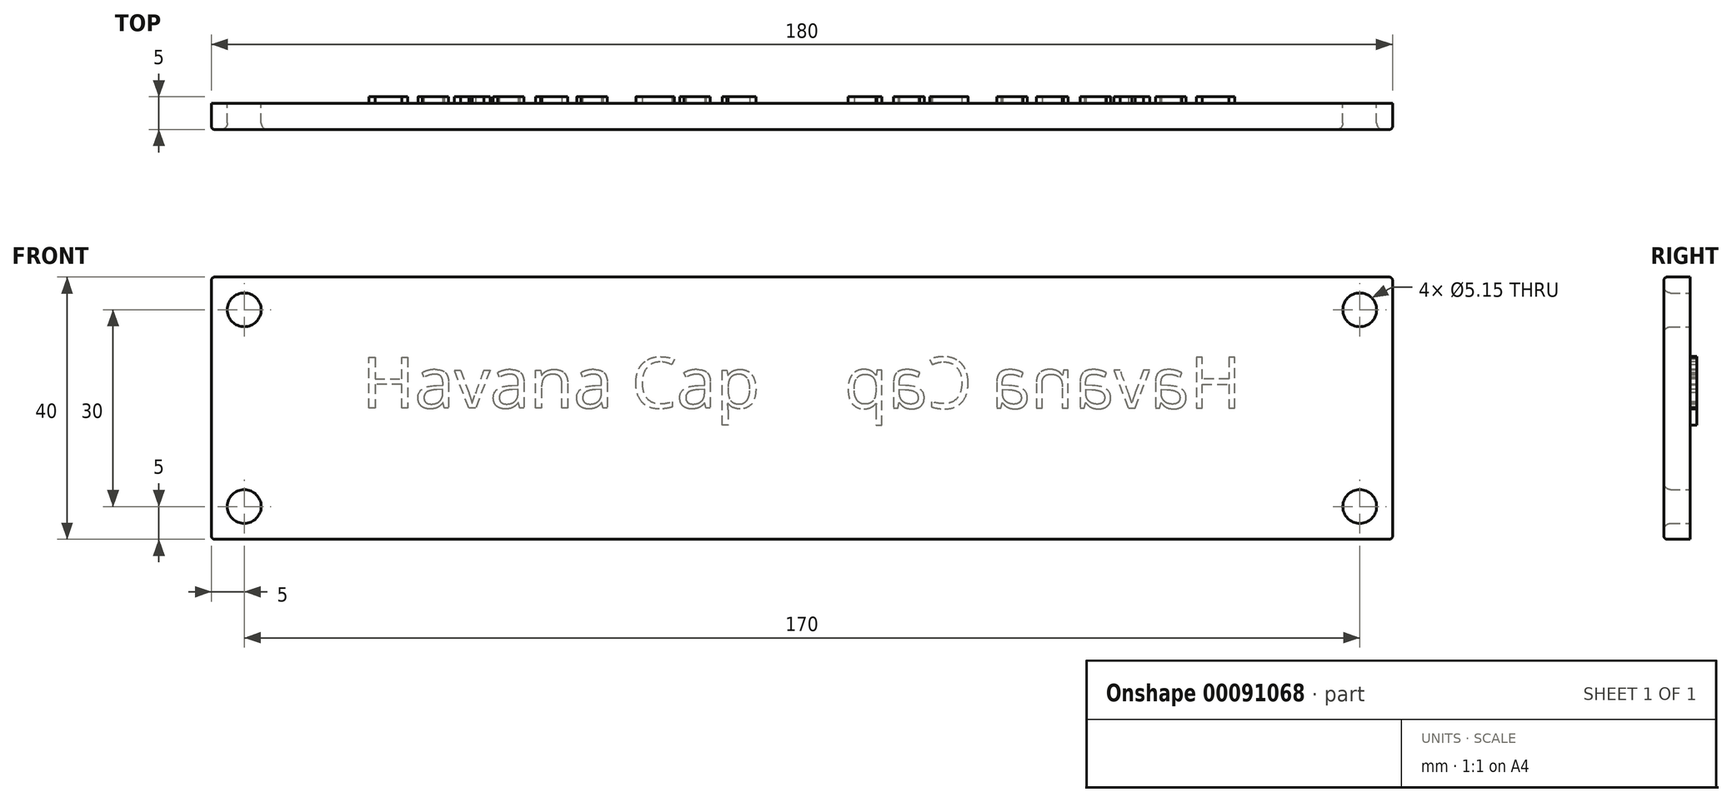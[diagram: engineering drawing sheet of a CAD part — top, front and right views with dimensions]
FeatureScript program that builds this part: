
annotation { "Feature Type Name" : "Feature", "Feature Type Description" : "" }
export const myFeature = defineFeature(function(context is Context, id is Id, definition is map)
    precondition{}
    {
        {
            var Q0;
            Q0=qCreatedBy(makeId("Front.planeOp"),FACE);
            var sketch = newSketch(context, id + "F0", { "sketchPlane" : qUnion([Q0])});
            skLineSegment(sketch, "E0.bottom", {"start": v(-90, -20) * mm, "end": v(90, -20) * mm});
            skLineSegment(sketch, "E0.top", {"start": v(-90, 20) * mm, "end": v(90, 20) * mm});
            skLineSegment(sketch, "E0.left", {"start": v(-90, -20) * mm, "end": v(-90, 20) * mm});
            skLineSegment(sketch, "E0.right", {"start": v(90, -20) * mm, "end": v(90, 20) * mm});
            skPoint(sketch, "E0.middle", {"position": v(0, 0) * mm});
            skCircle(sketch, "E1", {"center": v(-85, 15) * mm, "radius": 2.58 * mm});
            skPoint(sketch, "E2.start.orphan", {"position": v(-90, 0) * mm});
            skPoint(sketch, "E3.orphan", {"position": v(0, 20) * mm});
            skPoint(sketch, "E4.end.orphan", {"position": v(0, -20) * mm});
            skLineSegment(sketch, "E5", {"start": v(-90, 0) * mm, "end": v(0, 0) * mm, "construction": true});
            skLineSegment(sketch, "E6", {"start": v(0, 20) * mm, "end": v(0, -20) * mm, "construction": true});
            skCircle(sketch, "E7.MirrorC", {"center": v(-85, -15) * mm, "radius": 2.58 * mm});
            skCircle(sketch, "E8.MirrorC", {"center": v(85, 15) * mm, "radius": 2.58 * mm});
            skCircle(sketch, "E9.MirrorC", {"center": v(85, -15) * mm, "radius": 2.58 * mm});
            skSolve(sketch);
        }
        {
            var Q0;
            Q0=makeQuery(id+"F0.imprint","IMPRINT",FACE,{"disambiguationData":[TD([[makeQuery(id+"F0.imprint","IMPRINT",EDGE,{"derivedFrom":sQuery(id+"F0.wireOp",EDGE,"E0.bottom")}),1.0]])]});
            extrude(context, id + "F1", {"entities" : qUnion([Q0]), "depth" : 4 * mm});
        }
        {
            var Q0;
            Q0=makeQuery(id+"F1.opExtrude","CAP_EDGE",EDGE,{"disambiguationData":[OSD([sQuery(id+"F0.wireOp",EDGE,"E1")])],"isStart":false});
            var Q1;
            Q1=makeQuery(id+"F1.opExtrude","CAP_EDGE",EDGE,{"disambiguationData":[OSD([sQuery(id+"F0.wireOp",EDGE,"f5b72a5b-8583-449a-bdbf-9ac5a681e1fd0.MirrorC")])],"isStart":false});
            var Q2;
            Q2=makeQuery(id+"F1.opExtrude","CAP_EDGE",EDGE,{"disambiguationData":[OSD([sQuery(id+"F0.wireOp",EDGE,"2623e306-60f4-4522-aa65-1e3e8c2cf5b60.MirrorC")])],"isStart":false});
            var Q3;
            Q3=makeQuery(id+"F1.opExtrude","CAP_EDGE",EDGE,{"disambiguationData":[OSD([sQuery(id+"F0.wireOp",EDGE,"be81a34d-1d50-4ce7-a7a8-4484a1701fac0.MirrorC")])],"isStart":false});
            var Q4;
            Q4=makeQuery(id+"F1.opExtrude","CAP_EDGE",EDGE,{"disambiguationData":[OSD([sQuery(id+"F0.wireOp",EDGE,"E7.MirrorC")])],"isStart":false});
            var Q5;
            Q5=makeQuery(id+"F1.opExtrude","CAP_EDGE",EDGE,{"disambiguationData":[OSD([sQuery(id+"F0.wireOp",EDGE,"E8.MirrorC")])],"isStart":false});
            var Q6;
            Q6=makeQuery(id+"F1.opExtrude","CAP_EDGE",EDGE,{"disambiguationData":[OSD([sQuery(id+"F0.wireOp",EDGE,"E9.MirrorC")])],"isStart":false});
            fillet(context, id + "F2", {"entities" : qUnion([Q0, Q1, Q2, Q3, Q4, Q5, Q6]), "radius" : 1 * mm, "tangentPropagation" : true, "allowEdgeOverflow" : false});
        }
        {
            var Q0;
            Q0=makeQuery(id+"F1.opExtrude","CAP_EDGE",EDGE,{"disambiguationData":[OSD([sQuery(id+"F0.wireOp",EDGE,"E0.top")])],"isStart":false});
            var Q1;
            Q1=makeQuery(id+"F1.opExtrude","CAP_EDGE",EDGE,{"disambiguationData":[OSD([sQuery(id+"F0.wireOp",EDGE,"E0.left")])],"isStart":false});
            var Q2;
            Q2=makeQuery(id+"F1.opExtrude","CAP_EDGE",EDGE,{"disambiguationData":[OSD([sQuery(id+"F0.wireOp",EDGE,"E0.bottom")])],"isStart":false});
            var Q3;
            Q3=makeQuery(id+"F1.opExtrude","CAP_EDGE",EDGE,{"disambiguationData":[OSD([sQuery(id+"F0.wireOp",EDGE,"E0.right")])],"isStart":false});
            var Q4;
            Q4=makeQuery(id+"F1.opExtrude","SWEPT_EDGE",EDGE,{"disambiguationData":[OSD([sQuery(id+"F0.wireOp",EDGE,"E0.top"),sQuery(id+"F0.wireOp",EDGE,"E0.left")])]});
            var Q5;
            Q5=makeQuery(id+"F1.opExtrude","SWEPT_EDGE",EDGE,{"disambiguationData":[OSD([sQuery(id+"F0.wireOp",EDGE,"E0.bottom"),sQuery(id+"F0.wireOp",EDGE,"E0.left")])]});
            var Q6;
            Q6=makeQuery(id+"F1.opExtrude","SWEPT_EDGE",EDGE,{"disambiguationData":[OSD([sQuery(id+"F0.wireOp",EDGE,"E0.top"),sQuery(id+"F0.wireOp",EDGE,"E0.right")])]});
            var Q7;
            Q7=makeQuery(id+"F1.opExtrude","SWEPT_EDGE",EDGE,{"disambiguationData":[OSD([sQuery(id+"F0.wireOp",EDGE,"E0.bottom"),sQuery(id+"F0.wireOp",EDGE,"E0.right")])]});
            fillet(context, id + "F3", {"entities" : qUnion([Q0, Q1, Q2, Q3, Q4, Q5, Q6, Q7]), "radius" : .5 * mm, "tangentPropagation" : true, "allowEdgeOverflow" : false});
        }
        {
            var Q0;
            Q0=makeQuery(id+"F1.opExtrude","CAP_FACE",FACE,{"disambiguationData":[OSD([sQuery(id+"F0.wireOp",EDGE,"E0.bottom"),sQuery(id+"F0.wireOp",EDGE,"E0.top"),sQuery(id+"F0.wireOp",EDGE,"E0.left"),sQuery(id+"F0.wireOp",EDGE,"E0.right"),sQuery(id+"F0.wireOp",EDGE,"E1"),sQuery(id+"F0.wireOp",EDGE,"E7.MirrorC"),sQuery(id+"F0.wireOp",EDGE,"E8.MirrorC"),sQuery(id+"F0.wireOp",EDGE,"E9.MirrorC")])],"isStart":true});
            var sketch = newSketch(context, id + "F4", { "sketchPlane" : qUnion([Q0])});
            skText(sketch, "E10", { "text": "Havana Cap", "fontName": "OpenSans-Regular.ttf"});
            skLineSegment(sketch, "E11", {"start": v(0, 20) * mm, "end": v(0, -20) * mm, "construction": true});
            const initialGuessF4  = {"E10": [-0.06704, 0, 1, 0, 0.00782]};
            skSetInitialGuess(sketch, initialGuessF4);
            skSolve(sketch);
        }
        {
            var Q0;
            Q0=qSketchRegion(id+"F4",true);
            extrude(context, id + "F5", {"entities" : qUnion([Q0]), "operationType" : NewBodyOperationType.ADD, "depth" : 1 * mm});
        }
        {
            var Q0;
            Q0=makeQuery(id+"F1.opExtrude","SWEPT_BODY",BODY,{"disambiguationData":[OSD([sQuery(id+"F0.wireOp",EDGE,"E0.bottom"),sQuery(id+"F0.wireOp",EDGE,"E0.top"),sQuery(id+"F0.wireOp",EDGE,"E0.left"),sQuery(id+"F0.wireOp",EDGE,"E0.right"),sQuery(id+"F0.wireOp",EDGE,"E1"),sQuery(id+"F0.wireOp",EDGE,"E7.MirrorC"),sQuery(id+"F0.wireOp",EDGE,"E8.MirrorC"),sQuery(id+"F0.wireOp",EDGE,"E9.MirrorC")])]});
            var Q1;
            Q1=makeQuery(id+"F5.opExtrude","SWEPT_FACE",FACE,{"disambiguationData":[OSD([sQuery(id+"F4.wireOp",EDGE,"E10.sketch_text.stroke-94")])]});
            var Q2;
            Q2=makeQuery(id+"F5.opExtrude","SWEPT_FACE",FACE,{"disambiguationData":[OSD([sQuery(id+"F4.wireOp",EDGE,"E10.sketch_text.stroke-169")])]});
            var Q3;
            Q3=makeQuery(id+"F5.opExtrude","SWEPT_FACE",FACE,{"disambiguationData":[OSD([sQuery(id+"F4.wireOp",EDGE,"E10.sketch_text.stroke-185")])]});
            var Q4;
            Q4=makeQuery(id+"F5.opExtrude","SWEPT_FACE",FACE,{"disambiguationData":[OSD([sQuery(id+"F4.wireOp",EDGE,"E10.sketch_text.stroke-125")])]});
            var Q5;
            Q5=makeQuery(id+"F5.opExtrude","SWEPT_FACE",FACE,{"disambiguationData":[OSD([sQuery(id+"F4.wireOp",EDGE,"E10.sketch_text.stroke-155")])]});
            var Q6;
            Q6=makeQuery(id+"F5.opExtrude","SWEPT_FACE",FACE,{"disambiguationData":[OSD([sQuery(id+"F4.wireOp",EDGE,"E10.sketch_text.stroke-65")])]});
            var Q7;
            Q7=makeQuery(id+"F5.opExtrude","SWEPT_FACE",FACE,{"disambiguationData":[OSD([sQuery(id+"F4.wireOp",EDGE,"E10.sketch_text.stroke-81")])]});
            var Q8;
            Q8=makeQuery(id+"F5.opExtrude","SWEPT_FACE",FACE,{"disambiguationData":[OSD([sQuery(id+"F4.wireOp",EDGE,"E10.sketch_text.stroke-67")])]});
            var Q9;
            Q9=makeQuery(id+"F5.opExtrude","SWEPT_FACE",FACE,{"disambiguationData":[OSD([sQuery(id+"F4.wireOp",EDGE,"E10.sketch_text.stroke-99")])]});
            var Q10;
            Q10=makeQuery(id+"F5.opExtrude","SWEPT_FACE",FACE,{"disambiguationData":[OSD([sQuery(id+"F4.wireOp",EDGE,"E10.sketch_text.stroke-127")])]});
            var Q11;
            Q11=makeQuery(id+"F5.opExtrude","SWEPT_FACE",FACE,{"disambiguationData":[OSD([sQuery(id+"F4.wireOp",EDGE,"E10.sketch_text.stroke-10")])]});
            var Q12;
            Q12=makeQuery(id+"F5.opExtrude","CAP_FACE",FACE,{"disambiguationData":[OSD([sQuery(id+"F4.wireOp",EDGE,"E10.sketch_text.stroke-9"),sQuery(id+"F4.wireOp",EDGE,"E10.sketch_text.stroke-10"),sQuery(id+"F4.wireOp",EDGE,"E10.sketch_text.stroke-11"),sQuery(id+"F4.wireOp",EDGE,"E10.sketch_text.stroke-12")])],"isStart":false});
            var Q13;
            Q13=makeQuery(id+"F5.opExtrude","SWEPT_FACE",FACE,{"disambiguationData":[OSD([sQuery(id+"F4.wireOp",EDGE,"E10.sketch_text.stroke-154")])]});
            var Q14;
            Q14=makeQuery(id+"F5.opExtrude","SWEPT_FACE",FACE,{"disambiguationData":[OSD([sQuery(id+"F4.wireOp",EDGE,"E10.sketch_text.stroke-1")])]});
            var Q15;
            Q15=makeQuery(id+"F5.opExtrude","CAP_FACE",FACE,{"disambiguationData":[OSD([sQuery(id+"F4.wireOp",EDGE,"E10.sketch_text.stroke-124"),sQuery(id+"F4.wireOp",EDGE,"E10.sketch_text.stroke-125"),sQuery(id+"F4.wireOp",EDGE,"E10.sketch_text.stroke-126"),sQuery(id+"F4.wireOp",EDGE,"E10.sketch_text.stroke-127"),sQuery(id+"F4.wireOp",EDGE,"E10.sketch_text.stroke-128"),sQuery(id+"F4.wireOp",EDGE,"E10.sketch_text.stroke-129"),sQuery(id+"F4.wireOp",EDGE,"E10.sketch_text.stroke-130"),sQuery(id+"F4.wireOp",EDGE,"E10.sketch_text.stroke-131"),sQuery(id+"F4.wireOp",EDGE,"E10.sketch_text.stroke-132"),sQuery(id+"F4.wireOp",EDGE,"E10.sketch_text.stroke-133"),sQuery(id+"F4.wireOp",EDGE,"E10.sketch_text.stroke-134"),sQuery(id+"F4.wireOp",EDGE,"E10.sketch_text.stroke-135"),sQuery(id+"F4.wireOp",EDGE,"E10.sketch_text.stroke-136"),sQuery(id+"F4.wireOp",EDGE,"E10.sketch_text.stroke-137"),sQuery(id+"F4.wireOp",EDGE,"E10.sketch_text.stroke-138")])],"isStart":false});
            var Q16;
            Q16=makeQuery(id+"F5.opExtrude","CAP_FACE",FACE,{"disambiguationData":[OSD([sQuery(id+"F4.wireOp",EDGE,"E10.sketch_text.stroke-34"),sQuery(id+"F4.wireOp",EDGE,"E10.sketch_text.stroke-35"),sQuery(id+"F4.wireOp",EDGE,"E10.sketch_text.stroke-36"),sQuery(id+"F4.wireOp",EDGE,"E10.sketch_text.stroke-37"),sQuery(id+"F4.wireOp",EDGE,"E10.sketch_text.stroke-38"),sQuery(id+"F4.wireOp",EDGE,"E10.sketch_text.stroke-39"),sQuery(id+"F4.wireOp",EDGE,"E10.sketch_text.stroke-40"),sQuery(id+"F4.wireOp",EDGE,"E10.sketch_text.stroke-41"),sQuery(id+"F4.wireOp",EDGE,"E10.sketch_text.stroke-42"),sQuery(id+"F4.wireOp",EDGE,"E10.sketch_text.stroke-43"),sQuery(id+"F4.wireOp",EDGE,"E10.sketch_text.stroke-44"),sQuery(id+"F4.wireOp",EDGE,"E10.sketch_text.stroke-45"),sQuery(id+"F4.wireOp",EDGE,"E10.sketch_text.stroke-46"),sQuery(id+"F4.wireOp",EDGE,"E10.sketch_text.stroke-47"),sQuery(id+"F4.wireOp",EDGE,"E10.sketch_text.stroke-48"),sQuery(id+"F4.wireOp",EDGE,"E10.sketch_text.stroke-49"),sQuery(id+"F4.wireOp",EDGE,"E10.sketch_text.stroke-50"),sQuery(id+"F4.wireOp",EDGE,"E10.sketch_text.stroke-51"),sQuery(id+"F4.wireOp",EDGE,"E10.sketch_text.stroke-52"),sQuery(id+"F4.wireOp",EDGE,"E10.sketch_text.stroke-53"),sQuery(id+"F4.wireOp",EDGE,"E10.sketch_text.stroke-54"),sQuery(id+"F4.wireOp",EDGE,"E10.sketch_text.stroke-55"),sQuery(id+"F4.wireOp",EDGE,"E10.sketch_text.stroke-56"),sQuery(id+"F4.wireOp",EDGE,"E10.sketch_text.stroke-57"),sQuery(id+"F4.wireOp",EDGE,"E10.sketch_text.stroke-58"),sQuery(id+"F4.wireOp",EDGE,"E10.sketch_text.stroke-59"),sQuery(id+"F4.wireOp",EDGE,"E10.sketch_text.stroke-60")])],"isStart":false});
            var Q17;
            Q17=makeQuery(id+"F5.opExtrude","SWEPT_FACE",FACE,{"disambiguationData":[OSD([sQuery(id+"F4.wireOp",EDGE,"E10.sketch_text.stroke-50")])]});
            var Q18;
            Q18=makeQuery(id+"F5.opExtrude","SWEPT_FACE",FACE,{"disambiguationData":[OSD([sQuery(id+"F4.wireOp",EDGE,"E10.sketch_text.stroke-2")])]});
            var Q19;
            Q19=makeQuery(id+"F5.opExtrude","SWEPT_FACE",FACE,{"disambiguationData":[OSD([sQuery(id+"F4.wireOp",EDGE,"E10.sketch_text.stroke-3")])]});
            var Q20;
            Q20=makeQuery(id+"F5.opExtrude","SWEPT_FACE",FACE,{"disambiguationData":[OSD([sQuery(id+"F4.wireOp",EDGE,"E10.sketch_text.stroke-5")])]});
            var Q21;
            Q21=makeQuery(id+"F5.opExtrude","SWEPT_FACE",FACE,{"disambiguationData":[OSD([sQuery(id+"F4.wireOp",EDGE,"E10.sketch_text.stroke-8")])]});
            var Q22;
            Q22=makeQuery(id+"F5.opExtrude","SWEPT_FACE",FACE,{"disambiguationData":[OSD([sQuery(id+"F4.wireOp",EDGE,"E10.sketch_text.stroke-98")])]});
            var Q23;
            Q23=makeQuery(id+"F5.opExtrude","SWEPT_FACE",FACE,{"disambiguationData":[OSD([sQuery(id+"F4.wireOp",EDGE,"E10.sketch_text.stroke-66")])]});
            var Q24;
            Q24=makeQuery(id+"F5.opExtrude","SWEPT_FACE",FACE,{"disambiguationData":[OSD([sQuery(id+"F4.wireOp",EDGE,"E10.sketch_text.stroke-153")])]});
            var Q25;
            Q25=makeQuery(id+"F5.opExtrude","SWEPT_FACE",FACE,{"disambiguationData":[OSD([sQuery(id+"F4.wireOp",EDGE,"E10.sketch_text.stroke-126")])]});
            var Q26;
            Q26=makeQuery(id+"F5.opExtrude","SWEPT_FACE",FACE,{"disambiguationData":[OSD([sQuery(id+"F4.wireOp",EDGE,"E10.sketch_text.stroke-183")])]});
            var Q27;
            Q27=makeQuery(id+"F5.opExtrude","SWEPT_FACE",FACE,{"disambiguationData":[OSD([sQuery(id+"F4.wireOp",EDGE,"E10.sketch_text.stroke-109")])]});
            var Q28;
            Q28=makeQuery(id+"F5.opExtrude","SWEPT_FACE",FACE,{"disambiguationData":[OSD([sQuery(id+"F4.wireOp",EDGE,"E10.sketch_text.stroke-186")])]});
            var Q29;
            Q29=makeQuery(id+"F5.opExtrude","SWEPT_FACE",FACE,{"disambiguationData":[OSD([sQuery(id+"F4.wireOp",EDGE,"E10.sketch_text.stroke-79")])]});
            var Q30;
            Q30=makeQuery(id+"F5.opExtrude","SWEPT_FACE",FACE,{"disambiguationData":[OSD([sQuery(id+"F4.wireOp",EDGE,"E10.sketch_text.stroke-110")])]});
            var Q31;
            Q31=makeQuery(id+"F5.opExtrude","SWEPT_FACE",FACE,{"disambiguationData":[OSD([sQuery(id+"F4.wireOp",EDGE,"E10.sketch_text.stroke-38")])]});
            var Q32;
            Q32=makeQuery(id+"F5.opExtrude","SWEPT_FACE",FACE,{"disambiguationData":[OSD([sQuery(id+"F4.wireOp",EDGE,"E10.sketch_text.stroke-24")])]});
            var Q33;
            Q33=makeQuery(id+"F5.opExtrude","SWEPT_FACE",FACE,{"disambiguationData":[OSD([sQuery(id+"F4.wireOp",EDGE,"E10.sketch_text.stroke-12")])]});
            var Q34;
            Q34=makeQuery(id+"F5.opExtrude","SWEPT_FACE",FACE,{"disambiguationData":[OSD([sQuery(id+"F4.wireOp",EDGE,"E10.sketch_text.stroke-100")])]});
            var Q35;
            Q35=makeQuery(id+"F5.opExtrude","SWEPT_FACE",FACE,{"disambiguationData":[OSD([sQuery(id+"F4.wireOp",EDGE,"E10.sketch_text.stroke-158")])]});
            var Q36;
            Q36=makeQuery(id+"F5.opExtrude","SWEPT_FACE",FACE,{"disambiguationData":[OSD([sQuery(id+"F4.wireOp",EDGE,"E10.sketch_text.stroke-142")])]});
            var Q37;
            Q37=makeQuery(id+"F5.opExtrude","SWEPT_FACE",FACE,{"disambiguationData":[OSD([sQuery(id+"F4.wireOp",EDGE,"E10.sketch_text.stroke-54")])]});
            var Q38;
            Q38=makeQuery(id+"F5.opExtrude","SWEPT_FACE",FACE,{"disambiguationData":[OSD([sQuery(id+"F4.wireOp",EDGE,"E10.sketch_text.stroke-25")])]});
            var Q39;
            Q39=makeQuery(id+"F5.opExtrude","SWEPT_FACE",FACE,{"disambiguationData":[OSD([sQuery(id+"F4.wireOp",EDGE,"E10.sketch_text.stroke-101")])]});
            var Q40;
            Q40=makeQuery(id+"F5.opExtrude","SWEPT_FACE",FACE,{"disambiguationData":[OSD([sQuery(id+"F4.wireOp",EDGE,"E10.sketch_text.stroke-69")])]});
            var Q41;
            Q41=makeQuery(id+"F5.opExtrude","SWEPT_FACE",FACE,{"disambiguationData":[OSD([sQuery(id+"F4.wireOp",EDGE,"E10.sketch_text.stroke-159")])]});
            var Q42;
            Q42=makeQuery(id+"F5.opExtrude","SWEPT_FACE",FACE,{"disambiguationData":[OSD([sQuery(id+"F4.wireOp",EDGE,"E10.sketch_text.stroke-85")])]});
            var Q43;
            Q43=makeQuery(id+"F5.opExtrude","SWEPT_FACE",FACE,{"disambiguationData":[OSD([sQuery(id+"F4.wireOp",EDGE,"E10.sketch_text.stroke-173")])]});
            var Q44;
            Q44=makeQuery(id+"F5.opExtrude","SWEPT_FACE",FACE,{"disambiguationData":[OSD([sQuery(id+"F4.wireOp",EDGE,"E10.sketch_text.stroke-40")])]});
            var Q45;
            Q45=makeQuery(id+"F5.opExtrude","SWEPT_FACE",FACE,{"disambiguationData":[OSD([sQuery(id+"F4.wireOp",EDGE,"E10.sketch_text.stroke-102")])]});
            var Q46;
            Q46=makeQuery(id+"F5.opExtrude","SWEPT_FACE",FACE,{"disambiguationData":[OSD([sQuery(id+"F4.wireOp",EDGE,"E10.sketch_text.stroke-86")])]});
            var Q47;
            Q47=makeQuery(id+"F5.opExtrude","SWEPT_FACE",FACE,{"disambiguationData":[OSD([sQuery(id+"F4.wireOp",EDGE,"E10.sketch_text.stroke-130")])]});
            var Q48;
            Q48=makeQuery(id+"F5.opExtrude","SWEPT_FACE",FACE,{"disambiguationData":[OSD([sQuery(id+"F4.wireOp",EDGE,"E10.sketch_text.stroke-103")])]});
            var Q49;
            Q49=makeQuery(id+"F5.opExtrude","SWEPT_FACE",FACE,{"disambiguationData":[OSD([sQuery(id+"F4.wireOp",EDGE,"E10.sketch_text.stroke-87")])]});
            var Q50;
            Q50=makeQuery(id+"F5.opExtrude","SWEPT_FACE",FACE,{"disambiguationData":[OSD([sQuery(id+"F4.wireOp",EDGE,"E10.sketch_text.stroke-145")])]});
            var Q51;
            Q51=makeQuery(id+"F5.opExtrude","SWEPT_FACE",FACE,{"disambiguationData":[OSD([sQuery(id+"F4.wireOp",EDGE,"E10.sketch_text.stroke-131")])]});
            var Q52;
            Q52=makeQuery(id+"F5.opExtrude","SWEPT_FACE",FACE,{"disambiguationData":[OSD([sQuery(id+"F4.wireOp",EDGE,"E10.sketch_text.stroke-28")])]});
            var Q53;
            Q53=makeQuery(id+"F5.opExtrude","SWEPT_FACE",FACE,{"disambiguationData":[OSD([sQuery(id+"F4.wireOp",EDGE,"E10.sketch_text.stroke-14")])]});
            var Q54;
            Q54=makeQuery(id+"F5.opExtrude","SWEPT_FACE",FACE,{"disambiguationData":[OSD([sQuery(id+"F4.wireOp",EDGE,"E10.sketch_text.stroke-88")])]});
            var Q55;
            Q55=makeQuery(id+"F5.opExtrude","SWEPT_FACE",FACE,{"disambiguationData":[OSD([sQuery(id+"F4.wireOp",EDGE,"E10.sketch_text.stroke-162")])]});
            var Q56;
            Q56=makeQuery(id+"F5.opExtrude","SWEPT_FACE",FACE,{"disambiguationData":[OSD([sQuery(id+"F4.wireOp",EDGE,"E10.sketch_text.stroke-176")])]});
            var Q57;
            Q57=makeQuery(id+"F5.opExtrude","SWEPT_FACE",FACE,{"disambiguationData":[OSD([sQuery(id+"F4.wireOp",EDGE,"E10.sketch_text.stroke-73")])]});
            var Q58;
            Q58=makeQuery(id+"F5.opExtrude","SWEPT_FACE",FACE,{"disambiguationData":[OSD([sQuery(id+"F4.wireOp",EDGE,"E10.sketch_text.stroke-59")])]});
            var Q59;
            Q59=makeQuery(id+"F5.opExtrude","SWEPT_FACE",FACE,{"disambiguationData":[OSD([sQuery(id+"F4.wireOp",EDGE,"E10.sketch_text.stroke-133")])]});
            var Q60;
            Q60=makeQuery(id+"F5.opExtrude","SWEPT_FACE",FACE,{"disambiguationData":[OSD([sQuery(id+"F4.wireOp",EDGE,"E10.sketch_text.stroke-119")])]});
            var Q61;
            Q61=makeQuery(id+"F5.opExtrude","SWEPT_FACE",FACE,{"disambiguationData":[OSD([sQuery(id+"F4.wireOp",EDGE,"E10.sketch_text.stroke-74")])]});
            var Q62;
            Q62=makeQuery(id+"F5.opExtrude","SWEPT_FACE",FACE,{"disambiguationData":[OSD([sQuery(id+"F4.wireOp",EDGE,"E10.sketch_text.stroke-44")])]});
            var Q63;
            Q63=makeQuery(id+"F5.opExtrude","SWEPT_FACE",FACE,{"disambiguationData":[OSD([sQuery(id+"F4.wireOp",EDGE,"E10.sketch_text.stroke-120")])]});
            var Q64;
            Q64=makeQuery(id+"F5.opExtrude","SWEPT_FACE",FACE,{"disambiguationData":[OSD([sQuery(id+"F4.wireOp",EDGE,"E10.sketch_text.stroke-90")])]});
            var Q65;
            Q65=makeQuery(id+"F5.opExtrude","SWEPT_FACE",FACE,{"disambiguationData":[OSD([sQuery(id+"F4.wireOp",EDGE,"E10.sketch_text.stroke-178")])]});
            var Q66;
            Q66=makeQuery(id+"F5.opExtrude","SWEPT_FACE",FACE,{"disambiguationData":[OSD([sQuery(id+"F4.wireOp",EDGE,"E10.sketch_text.stroke-45")])]});
            var Q67;
            Q67=makeQuery(id+"F5.opExtrude","SWEPT_FACE",FACE,{"disambiguationData":[OSD([sQuery(id+"F4.wireOp",EDGE,"E10.sketch_text.stroke-31")])]});
            var Q68;
            Q68=makeQuery(id+"F5.opExtrude","SWEPT_FACE",FACE,{"disambiguationData":[OSD([sQuery(id+"F4.wireOp",EDGE,"E10.sketch_text.stroke-135")])]});
            var Q69;
            Q69=makeQuery(id+"F5.opExtrude","SWEPT_FACE",FACE,{"disambiguationData":[OSD([sQuery(id+"F4.wireOp",EDGE,"E10.sketch_text.stroke-179")])]});
            var Q70;
            Q70=makeQuery(id+"F5.opExtrude","SWEPT_FACE",FACE,{"disambiguationData":[OSD([sQuery(id+"F4.wireOp",EDGE,"E10.sketch_text.stroke-165")])]});
            var Q71;
            Q71=makeQuery(id+"F5.opExtrude","SWEPT_FACE",FACE,{"disambiguationData":[OSD([sQuery(id+"F4.wireOp",EDGE,"E10.sketch_text.stroke-149")])]});
            var Q72;
            Q72=makeQuery(id+"F5.opExtrude","SWEPT_FACE",FACE,{"disambiguationData":[OSD([sQuery(id+"F4.wireOp",EDGE,"E10.sketch_text.stroke-136")])]});
            var Q73;
            Q73=makeQuery(id+"F5.opExtrude","SWEPT_FACE",FACE,{"disambiguationData":[OSD([sQuery(id+"F4.wireOp",EDGE,"E10.sketch_text.stroke-122")])]});
            var Q74;
            Q74=makeQuery(id+"F5.opExtrude","SWEPT_FACE",FACE,{"disambiguationData":[OSD([sQuery(id+"F4.wireOp",EDGE,"E10.sketch_text.stroke-106")])]});
            var Q75;
            Q75=makeQuery(id+"F5.opExtrude","SWEPT_FACE",FACE,{"disambiguationData":[OSD([sQuery(id+"F4.wireOp",EDGE,"E10.sketch_text.stroke-180")])]});
            var Q76;
            Q76=makeQuery(id+"F5.opExtrude","SWEPT_FACE",FACE,{"disambiguationData":[OSD([sQuery(id+"F4.wireOp",EDGE,"E10.sketch_text.stroke-166")])]});
            var Q77;
            Q77=makeQuery(id+"F5.opExtrude","SWEPT_FACE",FACE,{"disambiguationData":[OSD([sQuery(id+"F4.wireOp",EDGE,"E10.sketch_text.stroke-150")])]});
            var Q78;
            Q78=makeQuery(id+"F5.opExtrude","SWEPT_FACE",FACE,{"disambiguationData":[OSD([sQuery(id+"F4.wireOp",EDGE,"E10.sketch_text.stroke-76")])]});
            var Q79;
            Q79=makeQuery(id+"F5.opExtrude","SWEPT_FACE",FACE,{"disambiguationData":[OSD([sQuery(id+"F4.wireOp",EDGE,"E10.sketch_text.stroke-32")])]});
            var Q80;
            Q80=makeQuery(id+"F5.opExtrude","SWEPT_FACE",FACE,{"disambiguationData":[OSD([sQuery(id+"F4.wireOp",EDGE,"E10.sketch_text.stroke-181")])]});
            var Q81;
            Q81=makeQuery(id+"F5.opExtrude","SWEPT_FACE",FACE,{"disambiguationData":[OSD([sQuery(id+"F4.wireOp",EDGE,"E10.sketch_text.stroke-47")])]});
            var Q82;
            Q82=makeQuery(id+"F5.opExtrude","SWEPT_FACE",FACE,{"disambiguationData":[OSD([sQuery(id+"F4.wireOp",EDGE,"E10.sketch_text.stroke-123")])]});
            var Q83;
            Q83=makeQuery(id+"F5.opExtrude","SWEPT_FACE",FACE,{"disambiguationData":[OSD([sQuery(id+"F4.wireOp",EDGE,"E10.sketch_text.stroke-107")])]});
            var Q84;
            Q84=makeQuery(id+"F5.opExtrude","SWEPT_FACE",FACE,{"disambiguationData":[OSD([sQuery(id+"F4.wireOp",EDGE,"E10.sketch_text.stroke-48")])]});
            var Q85;
            Q85=makeQuery(id+"F5.opExtrude","SWEPT_FACE",FACE,{"disambiguationData":[OSD([sQuery(id+"F4.wireOp",EDGE,"E10.sketch_text.stroke-124")])]});
            var Q86;
            Q86=makeQuery(id+"F5.opExtrude","SWEPT_FACE",FACE,{"disambiguationData":[OSD([sQuery(id+"F4.wireOp",EDGE,"E10.sketch_text.stroke-108")])]});
            var Q87;
            Q87=makeQuery(id+"F5.opExtrude","CAP_FACE",FACE,{"disambiguationData":[OSD([sQuery(id+"F4.wireOp",EDGE,"E10.sketch_text.stroke-139"),sQuery(id+"F4.wireOp",EDGE,"E10.sketch_text.stroke-140"),sQuery(id+"F4.wireOp",EDGE,"E10.sketch_text.stroke-141"),sQuery(id+"F4.wireOp",EDGE,"E10.sketch_text.stroke-142"),sQuery(id+"F4.wireOp",EDGE,"E10.sketch_text.stroke-143"),sQuery(id+"F4.wireOp",EDGE,"E10.sketch_text.stroke-144"),sQuery(id+"F4.wireOp",EDGE,"E10.sketch_text.stroke-145"),sQuery(id+"F4.wireOp",EDGE,"E10.sketch_text.stroke-146"),sQuery(id+"F4.wireOp",EDGE,"E10.sketch_text.stroke-147"),sQuery(id+"F4.wireOp",EDGE,"E10.sketch_text.stroke-148"),sQuery(id+"F4.wireOp",EDGE,"E10.sketch_text.stroke-149"),sQuery(id+"F4.wireOp",EDGE,"E10.sketch_text.stroke-150"),sQuery(id+"F4.wireOp",EDGE,"E10.sketch_text.stroke-151"),sQuery(id+"F4.wireOp",EDGE,"E10.sketch_text.stroke-152"),sQuery(id+"F4.wireOp",EDGE,"E10.sketch_text.stroke-153"),sQuery(id+"F4.wireOp",EDGE,"E10.sketch_text.stroke-154"),sQuery(id+"F4.wireOp",EDGE,"E10.sketch_text.stroke-155"),sQuery(id+"F4.wireOp",EDGE,"E10.sketch_text.stroke-156"),sQuery(id+"F4.wireOp",EDGE,"E10.sketch_text.stroke-157"),sQuery(id+"F4.wireOp",EDGE,"E10.sketch_text.stroke-158"),sQuery(id+"F4.wireOp",EDGE,"E10.sketch_text.stroke-159"),sQuery(id+"F4.wireOp",EDGE,"E10.sketch_text.stroke-160"),sQuery(id+"F4.wireOp",EDGE,"E10.sketch_text.stroke-161"),sQuery(id+"F4.wireOp",EDGE,"E10.sketch_text.stroke-162"),sQuery(id+"F4.wireOp",EDGE,"E10.sketch_text.stroke-163"),sQuery(id+"F4.wireOp",EDGE,"E10.sketch_text.stroke-164"),sQuery(id+"F4.wireOp",EDGE,"E10.sketch_text.stroke-165")])],"isStart":false});
            var Q88;
            Q88=makeQuery(id+"F5.opExtrude","CAP_FACE",FACE,{"disambiguationData":[OSD([sQuery(id+"F4.wireOp",EDGE,"E10.sketch_text.stroke-21"),sQuery(id+"F4.wireOp",EDGE,"E10.sketch_text.stroke-22"),sQuery(id+"F4.wireOp",EDGE,"E10.sketch_text.stroke-23"),sQuery(id+"F4.wireOp",EDGE,"E10.sketch_text.stroke-24"),sQuery(id+"F4.wireOp",EDGE,"E10.sketch_text.stroke-25"),sQuery(id+"F4.wireOp",EDGE,"E10.sketch_text.stroke-26"),sQuery(id+"F4.wireOp",EDGE,"E10.sketch_text.stroke-27"),sQuery(id+"F4.wireOp",EDGE,"E10.sketch_text.stroke-28"),sQuery(id+"F4.wireOp",EDGE,"E10.sketch_text.stroke-29"),sQuery(id+"F4.wireOp",EDGE,"E10.sketch_text.stroke-30"),sQuery(id+"F4.wireOp",EDGE,"E10.sketch_text.stroke-31"),sQuery(id+"F4.wireOp",EDGE,"E10.sketch_text.stroke-32"),sQuery(id+"F4.wireOp",EDGE,"E10.sketch_text.stroke-33")])],"isStart":false});
            var Q89;
            Q89=makeQuery(id+"F5.opExtrude","SWEPT_FACE",FACE,{"disambiguationData":[OSD([sQuery(id+"F4.wireOp",EDGE,"E10.sketch_text.stroke-113")])]});
            var Q90;
            Q90=makeQuery(id+"F5.opExtrude","SWEPT_FACE",FACE,{"disambiguationData":[OSD([sQuery(id+"F4.wireOp",EDGE,"E10.sketch_text.stroke-37")])]});
            var Q91;
            Q91=makeQuery(id+"F5.opExtrude","SWEPT_FACE",FACE,{"disambiguationData":[OSD([sQuery(id+"F4.wireOp",EDGE,"E10.sketch_text.stroke-187")])]});
            var Q92;
            Q92=makeQuery(id+"F5.opExtrude","SWEPT_FACE",FACE,{"disambiguationData":[OSD([sQuery(id+"F4.wireOp",EDGE,"E10.sketch_text.stroke-0")])]});
            var Q93;
            Q93=makeQuery(id+"F5.opExtrude","SWEPT_FACE",FACE,{"disambiguationData":[OSD([sQuery(id+"F4.wireOp",EDGE,"E10.sketch_text.stroke-4")])]});
            var Q94;
            Q94=makeQuery(id+"F5.opExtrude","SWEPT_FACE",FACE,{"disambiguationData":[OSD([sQuery(id+"F4.wireOp",EDGE,"E10.sketch_text.stroke-82")])]});
            var Q95;
            Q95=makeQuery(id+"F5.opExtrude","SWEPT_FACE",FACE,{"disambiguationData":[OSD([sQuery(id+"F4.wireOp",EDGE,"E10.sketch_text.stroke-52")])]});
            var Q96;
            Q96=makeQuery(id+"F5.opExtrude","SWEPT_FACE",FACE,{"disambiguationData":[OSD([sQuery(id+"F4.wireOp",EDGE,"E10.sketch_text.stroke-49")])]});
            var Q97;
            Q97=makeQuery(id+"F5.opExtrude","SWEPT_FACE",FACE,{"disambiguationData":[OSD([sQuery(id+"F4.wireOp",EDGE,"E10.sketch_text.stroke-63")])]});
            var Q98;
            Q98=makeQuery(id+"F5.opExtrude","SWEPT_FACE",FACE,{"disambiguationData":[OSD([sQuery(id+"F4.wireOp",EDGE,"E10.sketch_text.stroke-21")])]});
            var Q99;
            Q99=makeQuery(id+"F5.opExtrude","SWEPT_FACE",FACE,{"disambiguationData":[OSD([sQuery(id+"F4.wireOp",EDGE,"E10.sketch_text.stroke-128")])]});
            var Q100;
            Q100=makeQuery(id+"F5.opExtrude","SWEPT_FACE",FACE,{"disambiguationData":[OSD([sQuery(id+"F4.wireOp",EDGE,"E10.sketch_text.stroke-55")])]});
            var Q101;
            Q101=makeQuery(id+"F5.opExtrude","SWEPT_FACE",FACE,{"disambiguationData":[OSD([sQuery(id+"F4.wireOp",EDGE,"E10.sketch_text.stroke-26")])]});
            var Q102;
            Q102=makeQuery(id+"F5.opExtrude","SWEPT_FACE",FACE,{"disambiguationData":[OSD([sQuery(id+"F4.wireOp",EDGE,"E10.sketch_text.stroke-174")])]});
            var Q103;
            Q103=makeQuery(id+"F5.opExtrude","SWEPT_FACE",FACE,{"disambiguationData":[OSD([sQuery(id+"F4.wireOp",EDGE,"E10.sketch_text.stroke-104")])]});
            var Q104;
            Q104=makeQuery(id+"F5.opExtrude","SWEPT_FACE",FACE,{"disambiguationData":[OSD([sQuery(id+"F4.wireOp",EDGE,"E10.sketch_text.stroke-72")])]});
            var Q105;
            Q105=makeQuery(id+"F5.opExtrude","SWEPT_FACE",FACE,{"disambiguationData":[OSD([sQuery(id+"F4.wireOp",EDGE,"E10.sketch_text.stroke-132")])]});
            var Q106;
            Q106=makeQuery(id+"F5.opExtrude","SWEPT_FACE",FACE,{"disambiguationData":[OSD([sQuery(id+"F4.wireOp",EDGE,"E10.sketch_text.stroke-43")])]});
            var Q107;
            Q107=makeQuery(id+"F5.opExtrude","SWEPT_FACE",FACE,{"disambiguationData":[OSD([sQuery(id+"F4.wireOp",EDGE,"E10.sketch_text.stroke-15")])]});
            var Q108;
            Q108=makeQuery(id+"F5.opExtrude","SWEPT_FACE",FACE,{"disambiguationData":[OSD([sQuery(id+"F4.wireOp",EDGE,"E10.sketch_text.stroke-89")])]});
            var Q109;
            Q109=makeQuery(id+"F5.opExtrude","SWEPT_FACE",FACE,{"disambiguationData":[OSD([sQuery(id+"F4.wireOp",EDGE,"E10.sketch_text.stroke-163")])]});
            var Q110;
            Q110=makeQuery(id+"F5.opExtrude","SWEPT_FACE",FACE,{"disambiguationData":[OSD([sQuery(id+"F4.wireOp",EDGE,"E10.sketch_text.stroke-30")])]});
            var Q111;
            Q111=makeQuery(id+"F5.opExtrude","SWEPT_FACE",FACE,{"disambiguationData":[OSD([sQuery(id+"F4.wireOp",EDGE,"E10.sketch_text.stroke-134")])]});
            var Q112;
            Q112=makeQuery(id+"F5.opExtrude","SWEPT_FACE",FACE,{"disambiguationData":[OSD([sQuery(id+"F4.wireOp",EDGE,"E10.sketch_text.stroke-121")])]});
            var Q113;
            Q113=makeQuery(id+"F5.opExtrude","CAP_FACE",FACE,{"disambiguationData":[OSD([sQuery(id+"F4.wireOp",EDGE,"E10.sketch_text.stroke-105"),sQuery(id+"F4.wireOp",EDGE,"E10.sketch_text.stroke-106"),sQuery(id+"F4.wireOp",EDGE,"E10.sketch_text.stroke-107"),sQuery(id+"F4.wireOp",EDGE,"E10.sketch_text.stroke-108"),sQuery(id+"F4.wireOp",EDGE,"E10.sketch_text.stroke-109"),sQuery(id+"F4.wireOp",EDGE,"E10.sketch_text.stroke-110"),sQuery(id+"F4.wireOp",EDGE,"E10.sketch_text.stroke-111"),sQuery(id+"F4.wireOp",EDGE,"E10.sketch_text.stroke-112"),sQuery(id+"F4.wireOp",EDGE,"E10.sketch_text.stroke-113"),sQuery(id+"F4.wireOp",EDGE,"E10.sketch_text.stroke-114"),sQuery(id+"F4.wireOp",EDGE,"E10.sketch_text.stroke-115"),sQuery(id+"F4.wireOp",EDGE,"E10.sketch_text.stroke-116"),sQuery(id+"F4.wireOp",EDGE,"E10.sketch_text.stroke-117"),sQuery(id+"F4.wireOp",EDGE,"E10.sketch_text.stroke-118"),sQuery(id+"F4.wireOp",EDGE,"E10.sketch_text.stroke-119"),sQuery(id+"F4.wireOp",EDGE,"E10.sketch_text.stroke-120"),sQuery(id+"F4.wireOp",EDGE,"E10.sketch_text.stroke-121"),sQuery(id+"F4.wireOp",EDGE,"E10.sketch_text.stroke-122"),sQuery(id+"F4.wireOp",EDGE,"E10.sketch_text.stroke-123")])],"isStart":false});
            var Q114;
            Q114=makeQuery(id+"F5.opExtrude","SWEPT_FACE",FACE,{"disambiguationData":[OSD([sQuery(id+"F4.wireOp",EDGE,"E10.sketch_text.stroke-92")])]});
            var Q115;
            Q115=makeQuery(id+"F5.opExtrude","SWEPT_FACE",FACE,{"disambiguationData":[OSD([sQuery(id+"F4.wireOp",EDGE,"E10.sketch_text.stroke-46")])]});
            var Q116;
            Q116=makeQuery(id+"F5.opExtrude","CAP_FACE",FACE,{"disambiguationData":[OSD([sQuery(id+"F4.wireOp",EDGE,"E10.sketch_text.stroke-61"),sQuery(id+"F4.wireOp",EDGE,"E10.sketch_text.stroke-62"),sQuery(id+"F4.wireOp",EDGE,"E10.sketch_text.stroke-63"),sQuery(id+"F4.wireOp",EDGE,"E10.sketch_text.stroke-64"),sQuery(id+"F4.wireOp",EDGE,"E10.sketch_text.stroke-65"),sQuery(id+"F4.wireOp",EDGE,"E10.sketch_text.stroke-66"),sQuery(id+"F4.wireOp",EDGE,"E10.sketch_text.stroke-67"),sQuery(id+"F4.wireOp",EDGE,"E10.sketch_text.stroke-68"),sQuery(id+"F4.wireOp",EDGE,"E10.sketch_text.stroke-69"),sQuery(id+"F4.wireOp",EDGE,"E10.sketch_text.stroke-70"),sQuery(id+"F4.wireOp",EDGE,"E10.sketch_text.stroke-71"),sQuery(id+"F4.wireOp",EDGE,"E10.sketch_text.stroke-72"),sQuery(id+"F4.wireOp",EDGE,"E10.sketch_text.stroke-73"),sQuery(id+"F4.wireOp",EDGE,"E10.sketch_text.stroke-74"),sQuery(id+"F4.wireOp",EDGE,"E10.sketch_text.stroke-75"),sQuery(id+"F4.wireOp",EDGE,"E10.sketch_text.stroke-76"),sQuery(id+"F4.wireOp",EDGE,"E10.sketch_text.stroke-77"),sQuery(id+"F4.wireOp",EDGE,"E10.sketch_text.stroke-78"),sQuery(id+"F4.wireOp",EDGE,"E10.sketch_text.stroke-79"),sQuery(id+"F4.wireOp",EDGE,"E10.sketch_text.stroke-80"),sQuery(id+"F4.wireOp",EDGE,"E10.sketch_text.stroke-81"),sQuery(id+"F4.wireOp",EDGE,"E10.sketch_text.stroke-82"),sQuery(id+"F4.wireOp",EDGE,"E10.sketch_text.stroke-83"),sQuery(id+"F4.wireOp",EDGE,"E10.sketch_text.stroke-84"),sQuery(id+"F4.wireOp",EDGE,"E10.sketch_text.stroke-85"),sQuery(id+"F4.wireOp",EDGE,"E10.sketch_text.stroke-86"),sQuery(id+"F4.wireOp",EDGE,"E10.sketch_text.stroke-87"),sQuery(id+"F4.wireOp",EDGE,"E10.sketch_text.stroke-88"),sQuery(id+"F4.wireOp",EDGE,"E10.sketch_text.stroke-89"),sQuery(id+"F4.wireOp",EDGE,"E10.sketch_text.stroke-90"),sQuery(id+"F4.wireOp",EDGE,"E10.sketch_text.stroke-91"),sQuery(id+"F4.wireOp",EDGE,"E10.sketch_text.stroke-92"),sQuery(id+"F4.wireOp",EDGE,"E10.sketch_text.stroke-93"),sQuery(id+"F4.wireOp",EDGE,"E10.sketch_text.stroke-94"),sQuery(id+"F4.wireOp",EDGE,"E10.sketch_text.stroke-95"),sQuery(id+"F4.wireOp",EDGE,"E10.sketch_text.stroke-96"),sQuery(id+"F4.wireOp",EDGE,"E10.sketch_text.stroke-97"),sQuery(id+"F4.wireOp",EDGE,"E10.sketch_text.stroke-98"),sQuery(id+"F4.wireOp",EDGE,"E10.sketch_text.stroke-99"),sQuery(id+"F4.wireOp",EDGE,"E10.sketch_text.stroke-100"),sQuery(id+"F4.wireOp",EDGE,"E10.sketch_text.stroke-101"),sQuery(id+"F4.wireOp",EDGE,"E10.sketch_text.stroke-102"),sQuery(id+"F4.wireOp",EDGE,"E10.sketch_text.stroke-103"),sQuery(id+"F4.wireOp",EDGE,"E10.sketch_text.stroke-104")])],"isStart":false});
            var Q117;
            Q117=makeQuery(id+"F5.opExtrude","SWEPT_FACE",FACE,{"disambiguationData":[OSD([sQuery(id+"F4.wireOp",EDGE,"E10.sketch_text.stroke-33")])]});
            var Q118;
            Q118=makeQuery(id+"F5.opExtrude","SWEPT_FACE",FACE,{"disambiguationData":[OSD([sQuery(id+"F4.wireOp",EDGE,"E10.sketch_text.stroke-93")])]});
            var Q119;
            Q119=makeQuery(id+"F5.opExtrude","SWEPT_FACE",FACE,{"disambiguationData":[OSD([sQuery(id+"F4.wireOp",EDGE,"E10.sketch_text.stroke-34")])]});
            var Q120;
            Q120=makeQuery(id+"F5.opExtrude","SWEPT_FACE",FACE,{"disambiguationData":[OSD([sQuery(id+"F4.wireOp",EDGE,"E10.sketch_text.stroke-152")])]});
            var Q121;
            Q121=makeQuery(id+"F5.opExtrude","SWEPT_FACE",FACE,{"disambiguationData":[OSD([sQuery(id+"F4.wireOp",EDGE,"E10.sketch_text.stroke-51")])]});
            var Q122;
            Q122=makeQuery(id+"F5.opExtrude","SWEPT_FACE",FACE,{"disambiguationData":[OSD([sQuery(id+"F4.wireOp",EDGE,"E10.sketch_text.stroke-6")])]});
            var Q123;
            Q123=makeQuery(id+"F5.opExtrude","SWEPT_FACE",FACE,{"disambiguationData":[OSD([sQuery(id+"F4.wireOp",EDGE,"E10.sketch_text.stroke-7")])]});
            var Q124;
            Q124=makeQuery(id+"F5.opExtrude","SWEPT_FACE",FACE,{"disambiguationData":[OSD([sQuery(id+"F4.wireOp",EDGE,"E10.sketch_text.stroke-156")])]});
            var Q125;
            Q125=makeQuery(id+"F5.opExtrude","SWEPT_FACE",FACE,{"disambiguationData":[OSD([sQuery(id+"F4.wireOp",EDGE,"E10.sketch_text.stroke-112")])]});
            var Q126;
            Q126=makeQuery(id+"F5.boolean.opBoolean","SPLIT",FACE,{"disambiguationData":[TD([makeQuery(id+"F5.opExtrude","SWEPT_FACE",FACE,{"disambiguationData":[OSD([sQuery(id+"F4.wireOp",EDGE,"E10.sketch_text.stroke-182")])]})])],"derivedFrom":makeQuery(id+"F1.opExtrude","CAP_FACE",FACE,{"disambiguationData":[OSD([sQuery(id+"F0.wireOp",EDGE,"E0.bottom"),sQuery(id+"F0.wireOp",EDGE,"E0.top"),sQuery(id+"F0.wireOp",EDGE,"E0.left"),sQuery(id+"F0.wireOp",EDGE,"E0.right"),sQuery(id+"F0.wireOp",EDGE,"E1"),sQuery(id+"F0.wireOp",EDGE,"E7.MirrorC"),sQuery(id+"F0.wireOp",EDGE,"E8.MirrorC"),sQuery(id+"F0.wireOp",EDGE,"E9.MirrorC")])],"isStart":true})});
            var Q127;
            Q127=makeQuery(id+"F5.opExtrude","SWEPT_FACE",FACE,{"disambiguationData":[OSD([sQuery(id+"F4.wireOp",EDGE,"E10.sketch_text.stroke-96")])]});
            var Q128;
            Q128=makeQuery(id+"F5.opExtrude","SWEPT_FACE",FACE,{"disambiguationData":[OSD([sQuery(id+"F4.wireOp",EDGE,"E10.sketch_text.stroke-114")])]});
            var Q129;
            Q129=makeQuery(id+"F5.opExtrude","SWEPT_FACE",FACE,{"disambiguationData":[OSD([sQuery(id+"F4.wireOp",EDGE,"E10.sketch_text.stroke-39")])]});
            var Q130;
            Q130=makeQuery(id+"F5.opExtrude","SWEPT_FACE",FACE,{"disambiguationData":[OSD([sQuery(id+"F4.wireOp",EDGE,"E10.sketch_text.stroke-13")])]});
            var Q131;
            Q131=makeQuery(id+"F5.opExtrude","SWEPT_FACE",FACE,{"disambiguationData":[OSD([sQuery(id+"F4.wireOp",EDGE,"E10.sketch_text.stroke-115")])]});
            var Q132;
            Q132=makeQuery(id+"F5.opExtrude","SWEPT_FACE",FACE,{"disambiguationData":[OSD([sQuery(id+"F4.wireOp",EDGE,"E10.sketch_text.stroke-56")])]});
            var Q133;
            Q133=makeQuery(id+"F5.opExtrude","SWEPT_FACE",FACE,{"disambiguationData":[OSD([sQuery(id+"F4.wireOp",EDGE,"E10.sketch_text.stroke-144")])]});
            var Q134;
            Q134=makeQuery(id+"F5.opExtrude","SWEPT_FACE",FACE,{"disambiguationData":[OSD([sQuery(id+"F4.wireOp",EDGE,"E10.sketch_text.stroke-190")])]});
            var Q135;
            Q135=makeQuery(id+"F5.opExtrude","SWEPT_FACE",FACE,{"disambiguationData":[OSD([sQuery(id+"F4.wireOp",EDGE,"E10.sketch_text.stroke-116")])]});
            var Q136;
            Q136=makeQuery(id+"F5.opExtrude","SWEPT_FACE",FACE,{"disambiguationData":[OSD([sQuery(id+"F4.wireOp",EDGE,"E10.sketch_text.stroke-41")])]});
            var Q137;
            Q137=makeQuery(id+"F5.opExtrude","SWEPT_FACE",FACE,{"disambiguationData":[OSD([sQuery(id+"F4.wireOp",EDGE,"E10.sketch_text.stroke-161")])]});
            var Q138;
            Q138=makeQuery(id+"F5.opExtrude","SWEPT_FACE",FACE,{"disambiguationData":[OSD([sQuery(id+"F4.wireOp",EDGE,"E10.sketch_text.stroke-146")])]});
            var Q139;
            Q139=makeQuery(id+"F5.opExtrude","SWEPT_FACE",FACE,{"disambiguationData":[OSD([sQuery(id+"F4.wireOp",EDGE,"E10.sketch_text.stroke-58")])]});
            var Q140;
            Q140=makeQuery(id+"F5.opExtrude","SWEPT_FACE",FACE,{"disambiguationData":[OSD([sQuery(id+"F4.wireOp",EDGE,"E10.sketch_text.stroke-105")])]});
            var Q141;
            Q141=makeQuery(id+"F5.opExtrude","SWEPT_FACE",FACE,{"disambiguationData":[OSD([sQuery(id+"F4.wireOp",EDGE,"E10.sketch_text.stroke-177")])]});
            var Q142;
            Q142=makeQuery(id+"F5.opExtrude","SWEPT_FACE",FACE,{"disambiguationData":[OSD([sQuery(id+"F4.wireOp",EDGE,"E10.sketch_text.stroke-77")])]});
            var Q143;
            Q143=makeQuery(id+"F5.opExtrude","SWEPT_FACE",FACE,{"disambiguationData":[OSD([sQuery(id+"F4.wireOp",EDGE,"E10.sketch_text.stroke-138")])]});
            var Q144;
            Q144=makeQuery(id+"F5.opExtrude","SWEPT_FACE",FACE,{"disambiguationData":[OSD([sQuery(id+"F4.wireOp",EDGE,"E10.sketch_text.stroke-111")])]});
            var Q145;
            Q145=makeQuery(id+"F5.opExtrude","SWEPT_FACE",FACE,{"disambiguationData":[OSD([sQuery(id+"F4.wireOp",EDGE,"E10.sketch_text.stroke-53")])]});
            var Q146;
            Q146=makeQuery(id+"F5.opExtrude","SWEPT_FACE",FACE,{"disambiguationData":[OSD([sQuery(id+"F4.wireOp",EDGE,"E10.sketch_text.stroke-141")])]});
            var Q147;
            Q147=makeQuery(id+"F5.opExtrude","SWEPT_FACE",FACE,{"disambiguationData":[OSD([sQuery(id+"F4.wireOp",EDGE,"E10.sketch_text.stroke-157")])]});
            var Q148;
            Q148=makeQuery(id+"F5.opExtrude","SWEPT_FACE",FACE,{"disambiguationData":[OSD([sQuery(id+"F4.wireOp",EDGE,"E10.sketch_text.stroke-64")])]});
            var Q149;
            Q149=makeQuery(id+"F5.boolean.opBoolean","SPLIT",FACE,{"disambiguationData":[TD([makeQuery(id+"F5.opExtrude","SWEPT_FACE",FACE,{"disambiguationData":[OSD([sQuery(id+"F4.wireOp",EDGE,"E10.sketch_text.stroke-53")])]})])],"derivedFrom":makeQuery(id+"F1.opExtrude","CAP_FACE",FACE,{"disambiguationData":[OSD([sQuery(id+"F0.wireOp",EDGE,"E0.bottom"),sQuery(id+"F0.wireOp",EDGE,"E0.top"),sQuery(id+"F0.wireOp",EDGE,"E0.left"),sQuery(id+"F0.wireOp",EDGE,"E0.right"),sQuery(id+"F0.wireOp",EDGE,"E1"),sQuery(id+"F0.wireOp",EDGE,"E7.MirrorC"),sQuery(id+"F0.wireOp",EDGE,"E8.MirrorC"),sQuery(id+"F0.wireOp",EDGE,"E9.MirrorC")])],"isStart":true})});
            var Q150;
            Q150=makeQuery(id+"F5.opExtrude","SWEPT_FACE",FACE,{"disambiguationData":[OSD([sQuery(id+"F4.wireOp",EDGE,"E10.sketch_text.stroke-36")])]});
            var Q151;
            Q151=makeQuery(id+"F5.opExtrude","SWEPT_FACE",FACE,{"disambiguationData":[OSD([sQuery(id+"F4.wireOp",EDGE,"E10.sketch_text.stroke-22")])]});
            var Q152;
            Q152=makeQuery(id+"F5.boolean.opBoolean","SPLIT",FACE,{"disambiguationData":[TD([makeQuery(id+"F5.opExtrude","SWEPT_FACE",FACE,{"disambiguationData":[OSD([sQuery(id+"F4.wireOp",EDGE,"E10.sketch_text.stroke-119")])]})])],"derivedFrom":makeQuery(id+"F1.opExtrude","CAP_FACE",FACE,{"disambiguationData":[OSD([sQuery(id+"F0.wireOp",EDGE,"E0.bottom"),sQuery(id+"F0.wireOp",EDGE,"E0.top"),sQuery(id+"F0.wireOp",EDGE,"E0.left"),sQuery(id+"F0.wireOp",EDGE,"E0.right"),sQuery(id+"F0.wireOp",EDGE,"E1"),sQuery(id+"F0.wireOp",EDGE,"E7.MirrorC"),sQuery(id+"F0.wireOp",EDGE,"E8.MirrorC"),sQuery(id+"F0.wireOp",EDGE,"E9.MirrorC")])],"isStart":true})});
            var Q153;
            Q153=makeQuery(id+"F5.boolean.opBoolean","SPLIT",FACE,{"disambiguationData":[TD([makeQuery(id+"F5.opExtrude","SWEPT_FACE",FACE,{"disambiguationData":[OSD([sQuery(id+"F4.wireOp",EDGE,"E10.sketch_text.stroke-158")])]})])],"derivedFrom":makeQuery(id+"F1.opExtrude","CAP_FACE",FACE,{"disambiguationData":[OSD([sQuery(id+"F0.wireOp",EDGE,"E0.bottom"),sQuery(id+"F0.wireOp",EDGE,"E0.top"),sQuery(id+"F0.wireOp",EDGE,"E0.left"),sQuery(id+"F0.wireOp",EDGE,"E0.right"),sQuery(id+"F0.wireOp",EDGE,"E1"),sQuery(id+"F0.wireOp",EDGE,"E7.MirrorC"),sQuery(id+"F0.wireOp",EDGE,"E8.MirrorC"),sQuery(id+"F0.wireOp",EDGE,"E9.MirrorC")])],"isStart":true})});
            var Q154;
            Q154=makeQuery(id+"F5.opExtrude","SWEPT_FACE",FACE,{"disambiguationData":[OSD([sQuery(id+"F4.wireOp",EDGE,"E10.sketch_text.stroke-9")])]});
            var Q155;
            Q155=makeQuery(id+"F5.opExtrude","SWEPT_FACE",FACE,{"disambiguationData":[OSD([sQuery(id+"F4.wireOp",EDGE,"E10.sketch_text.stroke-167")])]});
            var Q156;
            Q156=makeQuery(id+"F5.opExtrude","SWEPT_FACE",FACE,{"disambiguationData":[OSD([sQuery(id+"F4.wireOp",EDGE,"E10.sketch_text.stroke-95")])]});
            var Q157;
            Q157=makeQuery(id+"F5.opExtrude","SWEPT_FACE",FACE,{"disambiguationData":[OSD([sQuery(id+"F4.wireOp",EDGE,"E10.sketch_text.stroke-184")])]});
            var Q158;
            Q158=makeQuery(id+"F5.opExtrude","SWEPT_FACE",FACE,{"disambiguationData":[OSD([sQuery(id+"F4.wireOp",EDGE,"E10.sketch_text.stroke-84")])]});
            var Q159;
            Q159=makeQuery(id+"F5.opExtrude","SWEPT_FACE",FACE,{"disambiguationData":[OSD([sQuery(id+"F4.wireOp",EDGE,"E10.sketch_text.stroke-68")])]});
            var Q160;
            Q160=makeQuery(id+"F5.opExtrude","SWEPT_FACE",FACE,{"disambiguationData":[OSD([sQuery(id+"F4.wireOp",EDGE,"E10.sketch_text.stroke-143")])]});
            var Q161;
            Q161=makeQuery(id+"F5.opExtrude","SWEPT_FACE",FACE,{"disambiguationData":[OSD([sQuery(id+"F4.wireOp",EDGE,"E10.sketch_text.stroke-189")])]});
            var Q162;
            Q162=makeQuery(id+"F5.opExtrude","CAP_FACE",FACE,{"disambiguationData":[OSD([sQuery(id+"F4.wireOp",EDGE,"E10.sketch_text.stroke-13"),sQuery(id+"F4.wireOp",EDGE,"E10.sketch_text.stroke-14"),sQuery(id+"F4.wireOp",EDGE,"E10.sketch_text.stroke-15"),sQuery(id+"F4.wireOp",EDGE,"E10.sketch_text.stroke-16"),sQuery(id+"F4.wireOp",EDGE,"E10.sketch_text.stroke-17"),sQuery(id+"F4.wireOp",EDGE,"E10.sketch_text.stroke-18"),sQuery(id+"F4.wireOp",EDGE,"E10.sketch_text.stroke-19"),sQuery(id+"F4.wireOp",EDGE,"E10.sketch_text.stroke-20")])],"isStart":false});
            var Q163;
            Q163=makeQuery(id+"F5.opExtrude","SWEPT_FACE",FACE,{"disambiguationData":[OSD([sQuery(id+"F4.wireOp",EDGE,"E10.sketch_text.stroke-57")])]});
            var Q164;
            Q164=makeQuery(id+"F5.opExtrude","SWEPT_FACE",FACE,{"disambiguationData":[OSD([sQuery(id+"F4.wireOp",EDGE,"E10.sketch_text.stroke-29")])]});
            var Q165;
            Q165=makeQuery(id+"F5.opExtrude","SWEPT_FACE",FACE,{"disambiguationData":[OSD([sQuery(id+"F4.wireOp",EDGE,"E10.sketch_text.stroke-60")])]});
            var Q166;
            Q166=makeQuery(id+"F5.opExtrude","SWEPT_FACE",FACE,{"disambiguationData":[OSD([sQuery(id+"F4.wireOp",EDGE,"E10.sketch_text.stroke-148")])]});
            var Q167;
            Q167=makeQuery(id+"F5.opExtrude","SWEPT_FACE",FACE,{"disambiguationData":[OSD([sQuery(id+"F4.wireOp",EDGE,"E10.sketch_text.stroke-75")])]});
            var Q168;
            Q168=makeQuery(id+"F5.opExtrude","SWEPT_FACE",FACE,{"disambiguationData":[OSD([sQuery(id+"F4.wireOp",EDGE,"E10.sketch_text.stroke-91")])]});
            var Q169;
            Q169=makeQuery(id+"F5.opExtrude","SWEPT_FACE",FACE,{"disambiguationData":[OSD([sQuery(id+"F4.wireOp",EDGE,"E10.sketch_text.stroke-78")])]});
            var Q170;
            Q170=makeQuery(id+"F5.opExtrude","SWEPT_FACE",FACE,{"disambiguationData":[OSD([sQuery(id+"F4.wireOp",EDGE,"E10.sketch_text.stroke-62")])]});
            var Q171;
            Q171=makeQuery(id+"F5.opExtrude","SWEPT_FACE",FACE,{"disambiguationData":[OSD([sQuery(id+"F4.wireOp",EDGE,"E10.sketch_text.stroke-182")])]});
            var Q172;
            Q172=makeQuery(id+"F5.opExtrude","SWEPT_FACE",FACE,{"disambiguationData":[OSD([sQuery(id+"F4.wireOp",EDGE,"E10.sketch_text.stroke-11")])]});
            var Q173;
            Q173=makeQuery(id+"F5.opExtrude","SWEPT_FACE",FACE,{"disambiguationData":[OSD([sQuery(id+"F4.wireOp",EDGE,"E10.sketch_text.stroke-97")])]});
            var Q174;
            Q174=makeQuery(id+"F5.opExtrude","SWEPT_FACE",FACE,{"disambiguationData":[OSD([sQuery(id+"F4.wireOp",EDGE,"E10.sketch_text.stroke-23")])]});
            var Q175;
            Q175=makeQuery(id+"F5.opExtrude","SWEPT_FACE",FACE,{"disambiguationData":[OSD([sQuery(id+"F4.wireOp",EDGE,"E10.sketch_text.stroke-80")])]});
            var Q176;
            Q176=makeQuery(id+"F5.boolean.opBoolean","SPLIT",FACE,{"disambiguationData":[TD([makeQuery(id+"F5.opExtrude","SWEPT_FACE",FACE,{"disambiguationData":[OSD([sQuery(id+"F4.wireOp",EDGE,"E10.sketch_text.stroke-99")])]})])],"derivedFrom":makeQuery(id+"F1.opExtrude","CAP_FACE",FACE,{"disambiguationData":[OSD([sQuery(id+"F0.wireOp",EDGE,"E0.bottom"),sQuery(id+"F0.wireOp",EDGE,"E0.top"),sQuery(id+"F0.wireOp",EDGE,"E0.left"),sQuery(id+"F0.wireOp",EDGE,"E0.right"),sQuery(id+"F0.wireOp",EDGE,"E1"),sQuery(id+"F0.wireOp",EDGE,"E7.MirrorC"),sQuery(id+"F0.wireOp",EDGE,"E8.MirrorC"),sQuery(id+"F0.wireOp",EDGE,"E9.MirrorC")])],"isStart":true})});
            var Q177;
            Q177=makeQuery(id+"F5.opExtrude","SWEPT_FACE",FACE,{"disambiguationData":[OSD([sQuery(id+"F4.wireOp",EDGE,"E10.sketch_text.stroke-168")])]});
            var Q178;
            Q178=makeQuery(id+"F5.opExtrude","SWEPT_FACE",FACE,{"disambiguationData":[OSD([sQuery(id+"F4.wireOp",EDGE,"E10.sketch_text.stroke-188")])]});
            var Q179;
            Q179=makeQuery(id+"F5.opExtrude","SWEPT_FACE",FACE,{"disambiguationData":[OSD([sQuery(id+"F4.wireOp",EDGE,"E10.sketch_text.stroke-129")])]});
            var Q180;
            Q180=makeQuery(id+"F5.opExtrude","SWEPT_FACE",FACE,{"disambiguationData":[OSD([sQuery(id+"F4.wireOp",EDGE,"E10.sketch_text.stroke-27")])]});
            var Q181;
            Q181=makeQuery(id+"F5.opExtrude","SWEPT_FACE",FACE,{"disambiguationData":[OSD([sQuery(id+"F4.wireOp",EDGE,"E10.sketch_text.stroke-175")])]});
            var Q182;
            Q182=makeQuery(id+"F5.opExtrude","SWEPT_FACE",FACE,{"disambiguationData":[OSD([sQuery(id+"F4.wireOp",EDGE,"E10.sketch_text.stroke-42")])]});
            var Q183;
            Q183=makeQuery(id+"F5.opExtrude","SWEPT_FACE",FACE,{"disambiguationData":[OSD([sQuery(id+"F4.wireOp",EDGE,"E10.sketch_text.stroke-118")])]});
            var Q184;
            Q184=makeQuery(id+"F5.opExtrude","SWEPT_FACE",FACE,{"disambiguationData":[OSD([sQuery(id+"F4.wireOp",EDGE,"E10.sketch_text.stroke-151")])]});
            var Q185;
            Q185=makeQuery(id+"F5.opExtrude","SWEPT_FACE",FACE,{"disambiguationData":[OSD([sQuery(id+"F4.wireOp",EDGE,"E10.sketch_text.stroke-137")])]});
            var Q186;
            Q186=makeQuery(id+"F5.opExtrude","SWEPT_FACE",FACE,{"disambiguationData":[OSD([sQuery(id+"F4.wireOp",EDGE,"E10.sketch_text.stroke-83")])]});
            var Q187;
            Q187=makeQuery(id+"F5.boolean.opBoolean","SPLIT",FACE,{"disambiguationData":[TD([makeQuery(id+"F5.opExtrude","SWEPT_FACE",FACE,{"disambiguationData":[OSD([sQuery(id+"F4.wireOp",EDGE,"E10.sketch_text.stroke-90")])]})])],"derivedFrom":makeQuery(id+"F1.opExtrude","CAP_FACE",FACE,{"disambiguationData":[OSD([sQuery(id+"F0.wireOp",EDGE,"E0.bottom"),sQuery(id+"F0.wireOp",EDGE,"E0.top"),sQuery(id+"F0.wireOp",EDGE,"E0.left"),sQuery(id+"F0.wireOp",EDGE,"E0.right"),sQuery(id+"F0.wireOp",EDGE,"E1"),sQuery(id+"F0.wireOp",EDGE,"E7.MirrorC"),sQuery(id+"F0.wireOp",EDGE,"E8.MirrorC"),sQuery(id+"F0.wireOp",EDGE,"E9.MirrorC")])],"isStart":true})});
            var Q188;
            Q188=makeQuery(id+"F5.opExtrude","SWEPT_FACE",FACE,{"disambiguationData":[OSD([sQuery(id+"F4.wireOp",EDGE,"E10.sketch_text.stroke-139")])]});
            var Q189;
            Q189=makeQuery(id+"F5.opExtrude","SWEPT_FACE",FACE,{"disambiguationData":[OSD([sQuery(id+"F4.wireOp",EDGE,"E10.sketch_text.stroke-70")])]});
            var Q190;
            Q190=makeQuery(id+"F5.opExtrude","SWEPT_FACE",FACE,{"disambiguationData":[OSD([sQuery(id+"F4.wireOp",EDGE,"E10.sketch_text.stroke-160")])]});
            var Q191;
            Q191=makeQuery(id+"F5.opExtrude","SWEPT_FACE",FACE,{"disambiguationData":[OSD([sQuery(id+"F4.wireOp",EDGE,"E10.sketch_text.stroke-71")])]});
            var Q192;
            Q192=makeQuery(id+"F5.opExtrude","SWEPT_FACE",FACE,{"disambiguationData":[OSD([sQuery(id+"F4.wireOp",EDGE,"E10.sketch_text.stroke-117")])]});
            var Q193;
            Q193=makeQuery(id+"F5.opExtrude","SWEPT_FACE",FACE,{"disambiguationData":[OSD([sQuery(id+"F4.wireOp",EDGE,"E10.sketch_text.stroke-147")])]});
            var Q194;
            Q194=makeQuery(id+"F5.opExtrude","SWEPT_FACE",FACE,{"disambiguationData":[OSD([sQuery(id+"F4.wireOp",EDGE,"E10.sketch_text.stroke-164")])]});
            var Q195;
            Q195=makeQuery(id+"F5.opExtrude","SWEPT_FACE",FACE,{"disambiguationData":[OSD([sQuery(id+"F4.wireOp",EDGE,"E10.sketch_text.stroke-61")])]});
            var Q196;
            Q196=makeQuery(id+"F5.opExtrude","SWEPT_FACE",FACE,{"disambiguationData":[OSD([sQuery(id+"F4.wireOp",EDGE,"E10.sketch_text.stroke-19")])]});
            var Q197;
            Q197=makeQuery(id+"F5.opExtrude","SWEPT_FACE",FACE,{"disambiguationData":[OSD([sQuery(id+"F4.wireOp",EDGE,"E10.sketch_text.stroke-35")])]});
            var Q198;
            Q198=makeQuery(id+"F5.opExtrude","SWEPT_FACE",FACE,{"disambiguationData":[OSD([sQuery(id+"F4.wireOp",EDGE,"E10.sketch_text.stroke-140")])]});
            var Q199;
            Q199=makeQuery(id+"F5.opExtrude","SWEPT_FACE",FACE,{"disambiguationData":[OSD([sQuery(id+"F4.wireOp",EDGE,"E10.sketch_text.stroke-20")])]});
            var Q200;
            Q200=makeQuery(id+"F5.opExtrude","SWEPT_FACE",FACE,{"disambiguationData":[OSD([sQuery(id+"F4.wireOp",EDGE,"E10.sketch_text.stroke-16")])]});
            var Q201;
            Q201=makeQuery(id+"F5.opExtrude","SWEPT_FACE",FACE,{"disambiguationData":[OSD([sQuery(id+"F4.wireOp",EDGE,"E10.sketch_text.stroke-18")])]});
            var Q202;
            Q202=makeQuery(id+"F5.opExtrude","SWEPT_FACE",FACE,{"disambiguationData":[OSD([sQuery(id+"F4.wireOp",EDGE,"E10.sketch_text.stroke-17")])]});
            var Q203;
            Q203=qCreatedBy(makeId("Right.planeOp"),FACE);
            mirror(context, id + "F6", {"operationType" : NewBodyOperationType.ADD, "entities" : qUnion([Q0]), "faces" : qUnion([Q1, Q2, Q3, Q4, Q5, Q6, Q7, Q8, Q9, Q10, Q11, Q12, Q13, Q14, Q15, Q16, Q17, Q18, Q19, Q20, Q21, Q22, Q23, Q24, Q25, Q26, Q27, Q28, Q29, Q30, Q31, Q32, Q33, Q34, Q35, Q36, Q37, Q38, Q39, Q40, Q41, Q42, Q43, Q44, Q45, Q46, Q47, Q48, Q49, Q50, Q51, Q52, Q53, Q54, Q55, Q56, Q57, Q58, Q59, Q60, Q61, Q62, Q63, Q64, Q65, Q66, Q67, Q68, Q69, Q70, Q71, Q72, Q73, Q74, Q75, Q76, Q77, Q78, Q79, Q80, Q81, Q82, Q83, Q84, Q85, Q86, Q87, Q88, Q89, Q90, Q91, Q92, Q93, Q94, Q95, Q96, Q97, Q98, Q99, Q100, Q101, Q102, Q103, Q104, Q105, Q106, Q107, Q108, Q109, Q110, Q111, Q112, Q113, Q114, Q115, Q116, Q117, Q118, Q119, Q120, Q121, Q122, Q123, Q124, Q125, Q126, Q127, Q128, Q129, Q130, Q131, Q132, Q133, Q134, Q135, Q136, Q137, Q138, Q139, Q140, Q141, Q142, Q143, Q144, Q145, Q146, Q147, Q148, Q149, Q150, Q151, Q152, Q153, Q154, Q155, Q156, Q157, Q158, Q159, Q160, Q161, Q162, Q163, Q164, Q165, Q166, Q167, Q168, Q169, Q170, Q171, Q172, Q173, Q174, Q175, Q176, Q177, Q178, Q179, Q180, Q181, Q182, Q183, Q184, Q185, Q186, Q187, Q188, Q189, Q190, Q191, Q192, Q193, Q194, Q195, Q196, Q197, Q198, Q199, Q200, Q201, Q202]), "mirrorPlane" : qUnion([Q203])});
        }
    });
